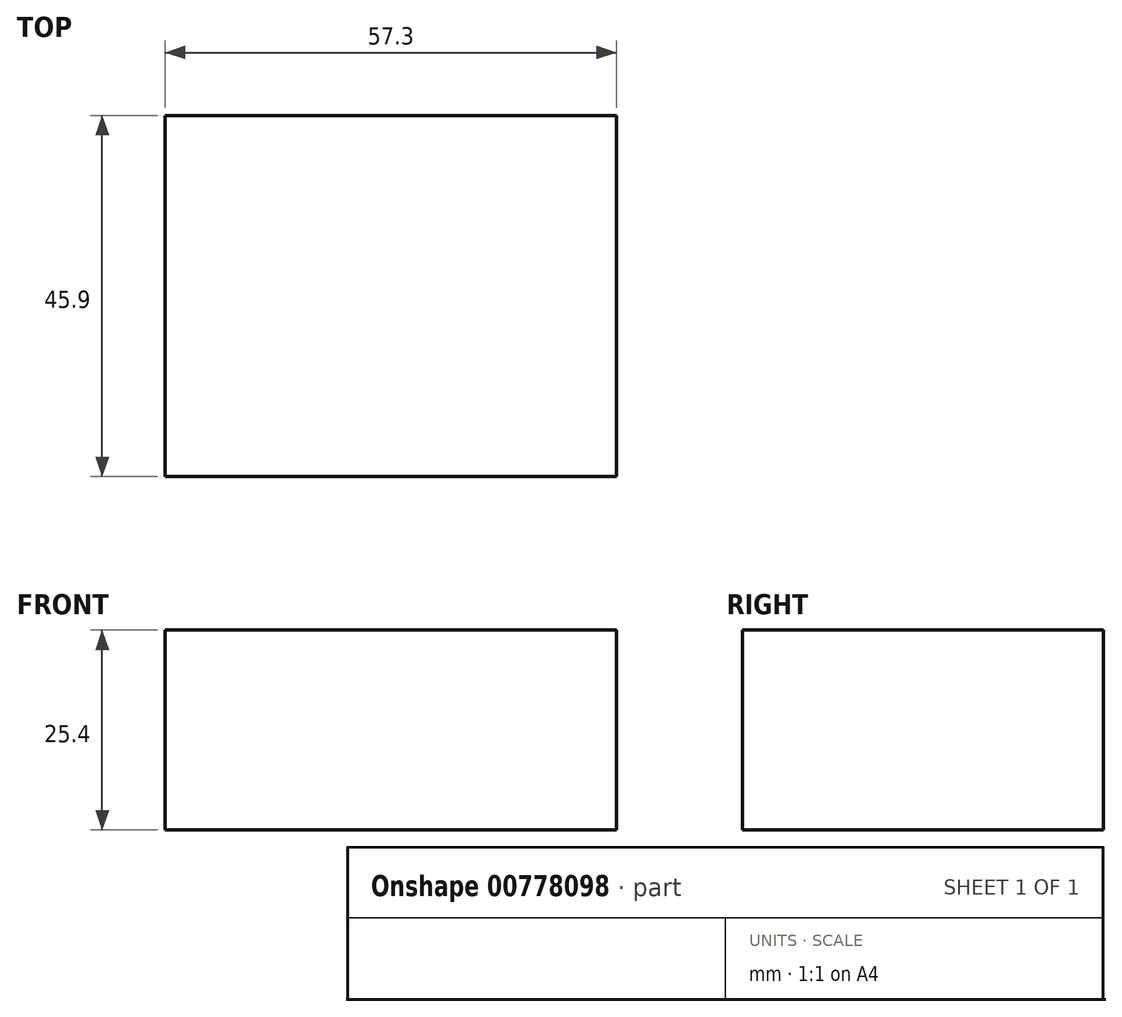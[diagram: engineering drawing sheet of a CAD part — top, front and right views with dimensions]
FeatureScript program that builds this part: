
annotation { "Feature Type Name" : "Feature", "Feature Type Description" : "" }
export const myFeature = defineFeature(function(context is Context, id is Id, definition is map)
    precondition{}
    {
        {
            var Q0;
            Q0=qCreatedBy(makeId("Top.planeOp"),FACE);
            var sketch = newSketch(context, id + "F0", { "sketchPlane" : qUnion([Q0])});
            skLineSegment(sketch, "E0.bottom", {"start": v(32.22, 24.78) * mm, "end": v(-25.08, 24.78) * mm});
            skLineSegment(sketch, "E0.top", {"start": v(32.22, -21.12) * mm, "end": v(-25.08, -21.12) * mm});
            skLineSegment(sketch, "E0.left", {"start": v(32.22, 24.78) * mm, "end": v(32.22, -21.12) * mm});
            skLineSegment(sketch, "E0.right", {"start": v(-25.08, 24.78) * mm, "end": v(-25.08, -21.12) * mm});
            skSolve(sketch);
        }
        {
            var Q0;
            Q0=makeQuery(id+"F0.imprint","IMPRINT",FACE,{"disambiguationData":[TD([[makeQuery(id+"F0.imprint","IMPRINT",EDGE,{"derivedFrom":sQuery(id+"F0.wireOp",EDGE,"E0.bottom")}),1.0]])]});
            extrude(context, id + "F1", {"entities" : qUnion([Q0]), "depth" : 25.4 * mm, "offsetDistance" : 25.4 * mm});
        }
    });
